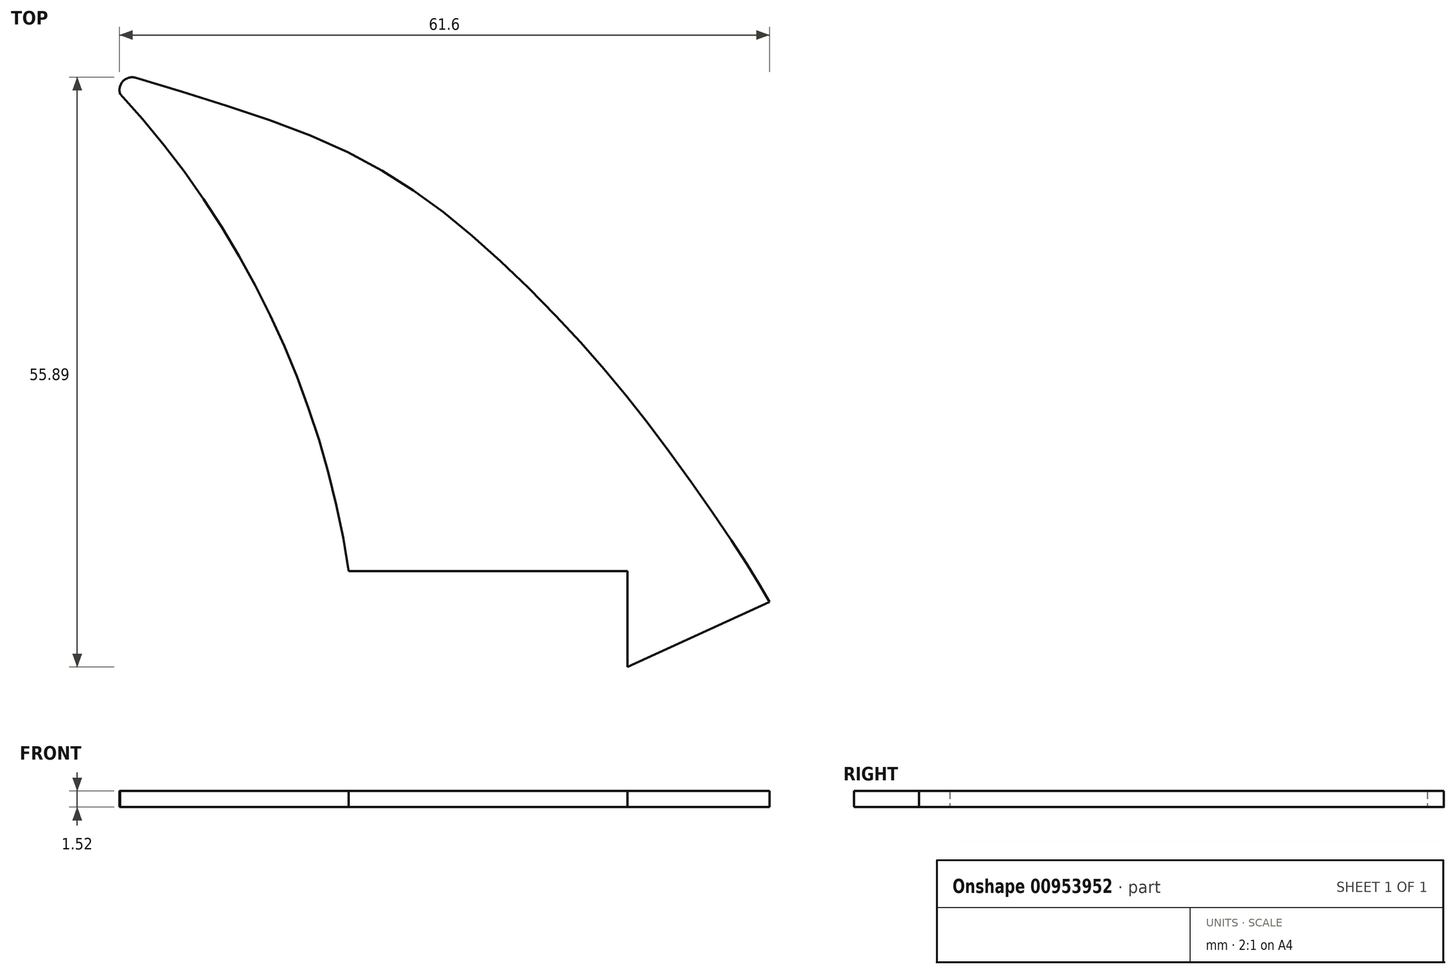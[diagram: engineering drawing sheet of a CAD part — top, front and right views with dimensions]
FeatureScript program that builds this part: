
annotation { "Feature Type Name" : "Feature", "Feature Type Description" : "" }
export const myFeature = defineFeature(function(context is Context, id is Id, definition is map)
    precondition{}
    {
        {
            var Q0;
            Q0=qCreatedBy(makeId("Top.planeOp"),FACE);
            var sketch = newSketch(context, id + "F0", { "sketchPlane" : qUnion([Q0])});
            skLineSegment(sketch, "E0", {"start": v(-75.55, 15.58) * mm, "end": v(-49.14, 15.58) * mm});
            skLineSegment(sketch, "E1", {"start": v(-49.14, 15.58) * mm, "end": v(-49.14, 6.5) * mm});
            skLineSegment(sketch, "E2", {"start": v(-49.14, 6.5) * mm, "end": v(-35.68, 12.67) * mm});
            skArc(sketch, "E3", {"start": v(-75.55, 15.58) * mm, "mid": v(-82.99, 39.83) * mm, "end": v(-97.23, 60.82) * mm});
            skFitSpline(sketch, "E4", {"points": [v(-95.7, 62.34) * mm, v(-76.12, 55.51) * mm, v(-64.24, 47.68) * mm, v(-53.62, 37.31) * mm, v(-45.79, 27.7) * mm, v(-38.46, 17.22) * mm, v(-35.68, 12.67) * mm], "startDerivative": vector(99.68, -29.78) * mm, "endDerivative": vector(22.16, -37.81) * mm});
            skArc(sketch, "E5", {"start": v(-95.7, 62.34) * mm, "mid": v(-96.92, 62.03) * mm, "end": v(-97.23, 60.82) * mm});
            skSolve(sketch);
        }
        {
            var Q0;
            Q0=makeQuery(id+"F0.imprint","IMPRINT",FACE,{"disambiguationData":[TD([[makeQuery(id+"F0.imprint","IMPRINT",EDGE,{"derivedFrom":sQuery(id+"F0.wireOp",EDGE,"E0")}),1.0]])]});
            extrude(context, id + "F1", {"entities" : qUnion([Q0]), "depth" : 1.52 * mm, "offsetDistance" : 25.4 * mm});
        }
    });
